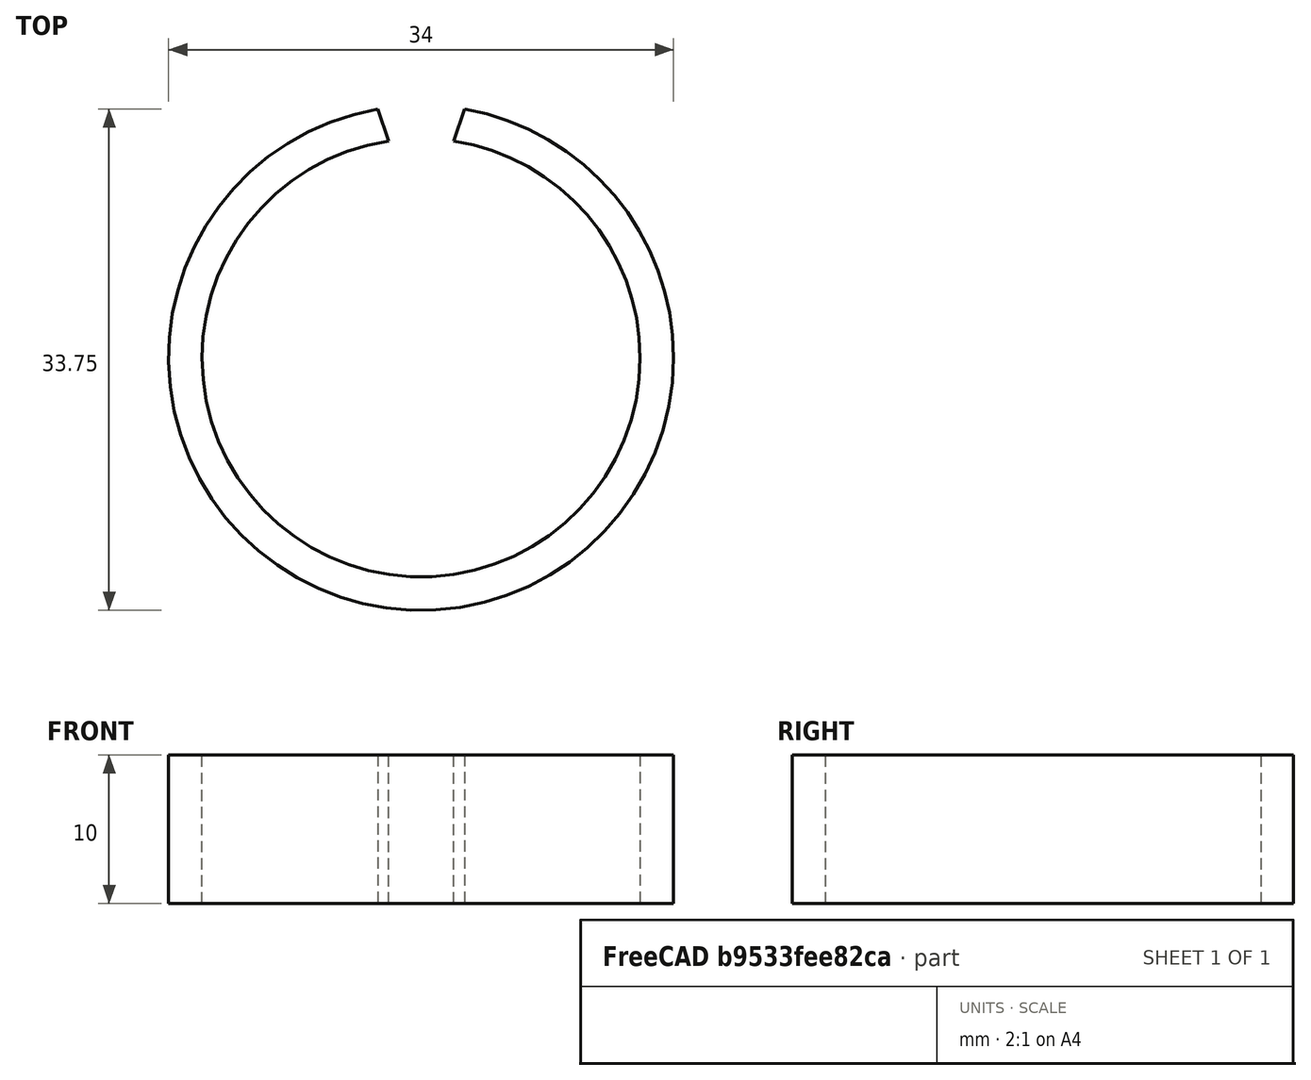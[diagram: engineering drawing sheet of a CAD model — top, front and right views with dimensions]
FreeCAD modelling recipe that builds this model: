
FCSTD DOCUMENT  (FreeCAD 0.18R16131 (Git))
Label: livecam_adapter_ring
License: All rights reserved
LicenseURL: http://en.wikipedia.org/wiki/All_rights_reserved
objects: Sketcher::SketchObject×3, PartDesign::Pad×2, PartDesign::Body×2, PartDesign::Pocket×1, Part::Cut×1
note: 12 computed .brp shape members not serialized (recipe doc carries the construction recipe); baked Part::Feature solids carry a one-line shape summary decoded from their .brp

FEATURE [Sketcher::SketchObject] Sketch
  MapMode = 5
  Support = -> [XY_Plane]
  sketch-geometry (1):
    g0: Circle CenterX=0 CenterY=0 CenterZ=0 NormalX=0 NormalY=0 NormalZ=1 AngleXU=0 Radius=17
FEATURE [PartDesign::Pad] Pad
  Length = 10
  Length2 = 100
  Profile = -> Sketch
  Type = 0
FEATURE [Sketcher::SketchObject] Sketch001
  MapMode = 5
  Placement = pos=(0,0,10) rot=(0,0,1;0rad)
  Support = -> [Pad]
  sketch-geometry (1):
    g0: Circle CenterX=0 CenterY=0 CenterZ=0 NormalX=0 NormalY=0 NormalZ=1 AngleXU=0 Radius=14.75
FEATURE [PartDesign::Pocket] Pocket
  BaseFeature = -> Pad
  Length = 10
  Length2 = 100
  Profile = -> Sketch001
  Type = 0
FEATURE [PartDesign::Body] Body  label="adapter ring"
  Group = -> [Sketch,Pad,Sketch001,Pocket]
  Origin = -> Origin
  Tip = -> Pocket
FEATURE [Sketcher::SketchObject] Sketch002
  MapMode = 5
  Support = -> [XY_Plane001]
  sketch-geometry (4):
    g0: LineSegment StartX=-3 StartY=17 StartZ=0 EndX=3 EndY=17 EndZ=0
    g1: LineSegment StartX=3 StartY=17 StartZ=0 EndX=2 EndY=14 EndZ=0
    g2: LineSegment StartX=2 StartY=14 StartZ=0 EndX=-2 EndY=14 EndZ=0
    g3: LineSegment StartX=-2 StartY=14 StartZ=0 EndX=-3 EndY=17 EndZ=0
  constraints (4):
    c: Coincident(g0,g1)
    c: Coincident(g1,g2)
    c: Coincident(g2,g3)
    c: Coincident(g3,g0)
FEATURE [PartDesign::Pad] Pad001
  Length = 10
  Length2 = 100
  Profile = -> Sketch002
  Type = 0
FEATURE [PartDesign::Body] Body001  label="adapter ring cutout"
  Group = -> [Sketch002,Pad001]
  Origin = -> Origin001
  Tip = -> Pad001
FEATURE [Part::Cut] Cut
  Base = -> Body
  Tool = -> Body001
